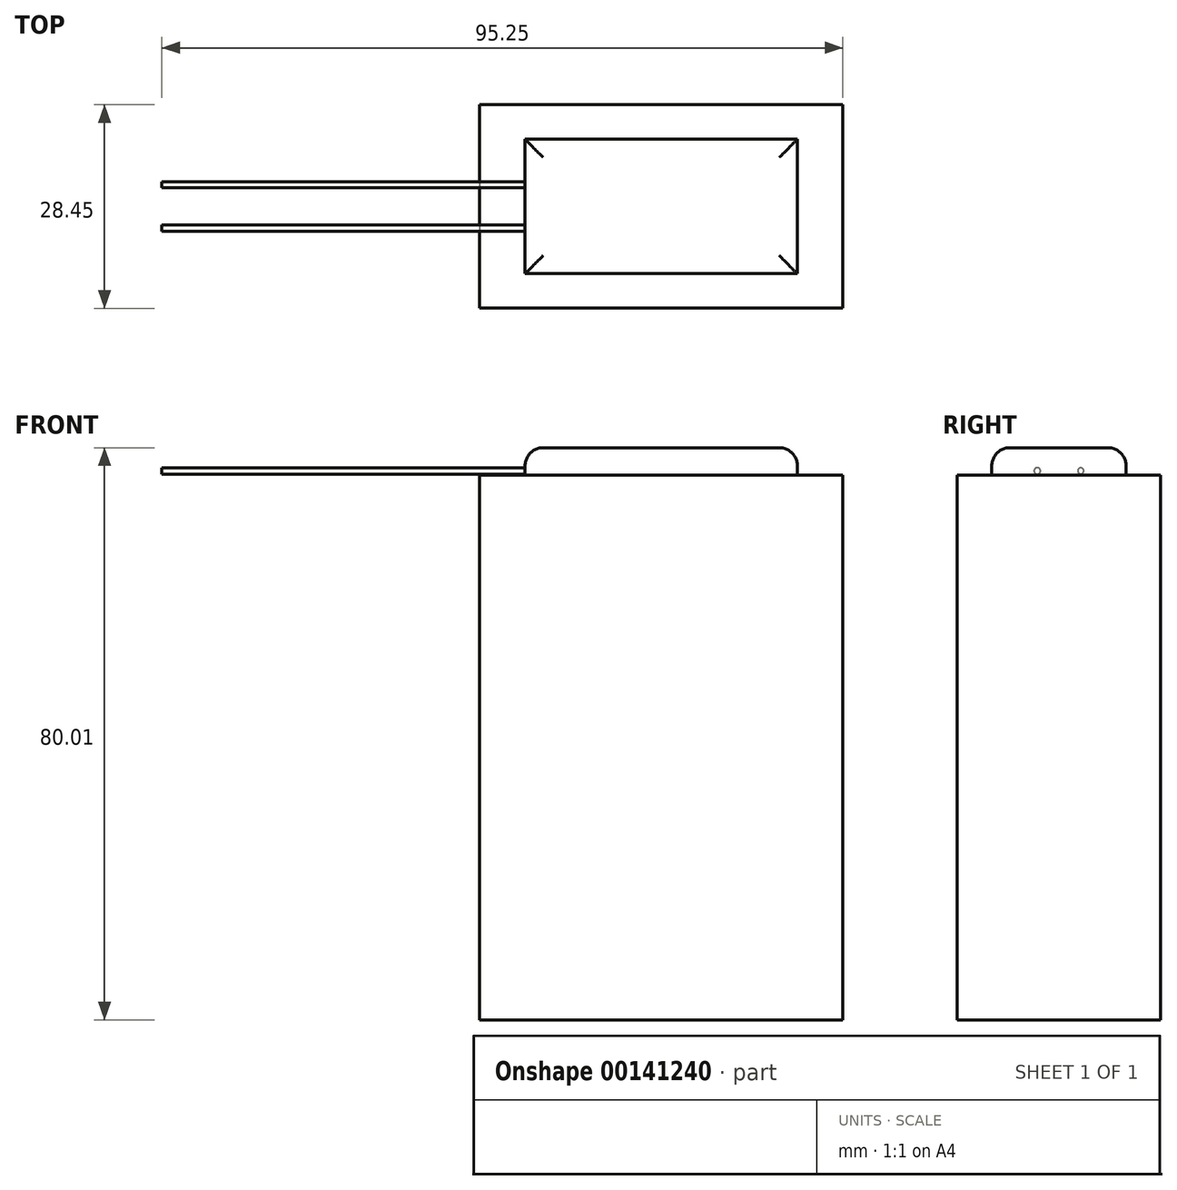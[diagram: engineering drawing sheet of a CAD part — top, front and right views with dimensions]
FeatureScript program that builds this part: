
annotation { "Feature Type Name" : "Feature", "Feature Type Description" : "" }
export const myFeature = defineFeature(function(context is Context, id is Id, definition is map)
    precondition{}
    {
        {
            var Q0;
            Q0=qCreatedBy(makeId("Top.planeOp"),FACE);
            var sketch = newSketch(context, id + "F0", { "sketchPlane" : qUnion([Q0])});
            skLineSegment(sketch, "E0.bottom", {"start": v(0, 0) * mm, "end": v(50.8, 0) * mm});
            skLineSegment(sketch, "E0.top", {"start": v(0, -28.45) * mm, "end": v(50.8, -28.45) * mm});
            skLineSegment(sketch, "E0.left", {"start": v(0, 0) * mm, "end": v(0, -28.45) * mm});
            skLineSegment(sketch, "E0.right", {"start": v(50.8, 0) * mm, "end": v(50.8, -28.45) * mm});
            skSolve(sketch);
        }
        {
            var Q0;
            Q0=makeQuery(id+"F0.imprint","IMPRINT",FACE,{"disambiguationData":[TD([[makeQuery(id+"F0.imprint","IMPRINT",EDGE,{"derivedFrom":sQuery(id+"F0.wireOp",EDGE,"E0.bottom")}),-1.0]])]});
            extrude(context, id + "F1", {"entities" : qUnion([Q0]), "depth" : 76.2 * mm});
        }
        {
            var Q0;
            Q0=makeQuery(id+"F1.opExtrude","CAP_FACE",FACE,{"disambiguationData":[OSD([sQuery(id+"F0.wireOp",EDGE,"E0.bottom"),sQuery(id+"F0.wireOp",EDGE,"E0.top"),sQuery(id+"F0.wireOp",EDGE,"E0.left"),sQuery(id+"F0.wireOp",EDGE,"E0.right")])],"isStart":false});
            var sketch = newSketch(context, id + "F2", { "sketchPlane" : qUnion([Q0])});
            skLineSegment(sketch, "E1.bottom", {"start": v(6.35, -4.83) * mm, "end": v(44.45, -4.83) * mm});
            skLineSegment(sketch, "E1.top", {"start": v(6.35, -23.62) * mm, "end": v(44.45, -23.62) * mm});
            skLineSegment(sketch, "E1.left", {"start": v(6.35, -4.83) * mm, "end": v(6.35, -23.62) * mm});
            skLineSegment(sketch, "E1.right", {"start": v(44.45, -4.83) * mm, "end": v(44.45, -23.62) * mm});
            skSolve(sketch);
        }
        {
            var Q0;
            Q0=makeQuery(id+"F2.imprint","IMPRINT",FACE,{"disambiguationData":[TD([[makeQuery(id+"F2.imprint","IMPRINT",EDGE,{"derivedFrom":sQuery(id+"F2.wireOp",EDGE,"E1.bottom")}),-1.0]])]});
            extrude(context, id + "F3", {"entities" : qUnion([Q0]), "operationType" : NewBodyOperationType.ADD, "depth" : 3.8 * mm});
        }
        {
            var Q0;
            Q0=makeQuery(id+"F3.opExtrude","CAP_EDGE",EDGE,{"disambiguationData":[OSD([sQuery(id+"F2.wireOp",EDGE,"E1.bottom")])],"isStart":false});
            var Q1;
            Q1=makeQuery(id+"F3.opExtrude","CAP_EDGE",EDGE,{"disambiguationData":[OSD([sQuery(id+"F2.wireOp",EDGE,"E1.top")])],"isStart":false});
            var Q2;
            Q2=makeQuery(id+"F3.opExtrude","CAP_EDGE",EDGE,{"disambiguationData":[OSD([sQuery(id+"F2.wireOp",EDGE,"E1.left")])],"isStart":false});
            var Q3;
            Q3=makeQuery(id+"F3.opExtrude","CAP_EDGE",EDGE,{"disambiguationData":[OSD([sQuery(id+"F2.wireOp",EDGE,"E1.right")])],"isStart":false});
            fillet(context, id + "F4", {"entities" : qUnion([Q0, Q1, Q2, Q3]), "radius" : 2.54 * mm, "tangentPropagation" : true, "allowEdgeOverflow" : false});
        }
        {
            var Q0;
            Q0=makeQuery(id+"F3.opExtrude","SWEPT_FACE",FACE,{"disambiguationData":[OSD([sQuery(id+"F2.wireOp",EDGE,"E1.left")])]});
            var sketch = newSketch(context, id + "F5", { "sketchPlane" : qUnion([Q0])});
            skCircle(sketch, "E2", {"center": v(11.17, 76.76) * mm, "radius": 0.42 * mm});
            skCircle(sketch, "E3", {"center": v(17.25, 76.76) * mm, "radius": 0.45 * mm});
            skSolve(sketch);
        }
        {
            var Q0;
            Q0=makeQuery(id+"F5.imprint","IMPRINT",FACE,{"disambiguationData":[TD([[makeQuery(id+"F5.imprint","IMPRINT",EDGE,{"derivedFrom":sQuery(id+"F5.wireOp",EDGE,"E2")}),1.0]])]});
            var Q1;
            Q1=makeQuery(id+"F5.imprint","IMPRINT",FACE,{"disambiguationData":[TD([[makeQuery(id+"F5.imprint","IMPRINT",EDGE,{"derivedFrom":sQuery(id+"F5.wireOp",EDGE,"E3")}),1.0]])]});
            extrude(context, id + "F6", {"entities" : qUnion([Q0, Q1]), "operationType" : NewBodyOperationType.ADD, "depth" : 50.8 * mm});
        }
    });
